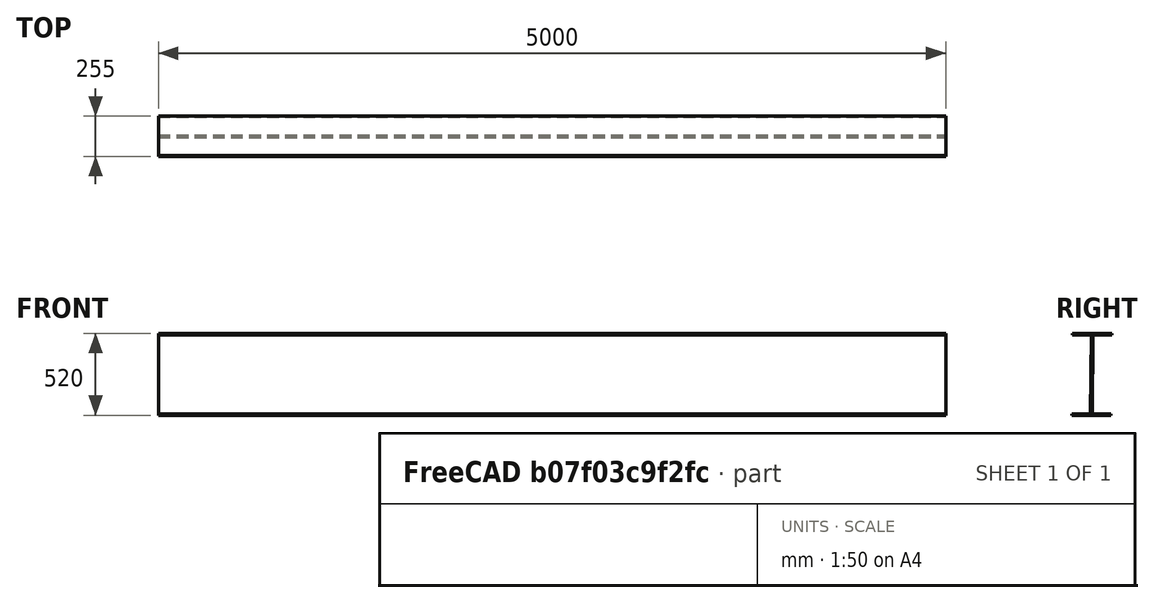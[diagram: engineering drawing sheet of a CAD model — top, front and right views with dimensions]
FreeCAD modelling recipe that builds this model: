
FCSTD DOCUMENT  (FreeCAD 0.21R33694 (Git))
Label: Plate_Girder
License: All rights reserved
LicenseURL: http://en.wikipedia.org/wiki/All_rights_reserved
objects: Sketcher::SketchObject×1, Part::Extrusion×1, Fem::ConstraintFixed×1, App::MaterialObjectPython×1, Fem::ConstraintForce×1, Fem::FemSolverObjectPython×1, Fem::FemMeshObjectPython×1, Fem::ConstraintDisplacement×1, Fem::FemAnalysis×1
note: 2 computed .brp shape members not serialized (recipe doc carries the construction recipe); baked Part::Feature solids carry a one-line shape summary decoded from their .brp

FEATURE [Sketcher::SketchObject] Sketch
  FullyConstrained = true
  Placement = pos=(0,0,0) rot=(0.57735,0.57735,0.57735;2.0944rad)
  sketch-geometry (16):
    g0: LineSegment StartX=0 StartY=0 StartZ=0 EndX=120 EndY=0 EndZ=0
    g1: LineSegment StartX=120 StartY=0 StartZ=0 EndX=125 EndY=500 EndZ=0
    g2: LineSegment StartX=125 StartY=500 StartZ=0 EndX=5 EndY=500 EndZ=0
    g3: LineSegment StartX=5 StartY=500 StartZ=0 EndX=5 EndY=510 EndZ=0
    g4: LineSegment StartX=255 StartY=510 StartZ=0 EndX=255 EndY=500 EndZ=0
    g5: LineSegment StartX=255 StartY=500 StartZ=0 EndX=135 EndY=500 EndZ=0
    g6: LineSegment StartX=135 StartY=500 StartZ=0 EndX=130 EndY=0 EndZ=0
    g7: LineSegment StartX=130 StartY=0 StartZ=0 EndX=250 EndY=0 EndZ=0
    g8: LineSegment StartX=250 StartY=0 StartZ=0 EndX=250 EndY=-10 EndZ=0
    g9: LineSegment StartX=0 StartY=-10 StartZ=0 EndX=0 EndY=0 EndZ=0
    g10: LineSegment StartX=250 StartY=-10 StartZ=0 EndX=130 EndY=-10 EndZ=0
    g11: LineSegment StartX=0 StartY=-10 StartZ=0 EndX=120 EndY=-10 EndZ=0
    g12: LineSegment StartX=120 StartY=-10 StartZ=0 EndX=130 EndY=-10 EndZ=0
    g13: LineSegment StartX=255 StartY=510 StartZ=0 EndX=135 EndY=510 EndZ=0
    g14: LineSegment StartX=135 StartY=510 StartZ=0 EndX=125 EndY=510 EndZ=0
    g15: LineSegment StartX=125 StartY=510 StartZ=0 EndX=5 EndY=510 EndZ=0
  constraints (47):
    c: Coincident(g-1,g0)
    c: Horizontal(g0)
    c: Coincident(g0,g1)
    c: Coincident(g1,g2)
    c: Horizontal(g2)
    c: Coincident(g2,g3)
    c: Vertical(g4)
    c: Coincident(g4,g5)
    c: Horizontal(g5)
    c: Coincident(g5,g6)
    c: PointOnObject(g6,g-1)
    c: Coincident(g6,g7)
    c: Coincident(g7,g8)
    c: Vertical(g8)
    c: PointOnObject(g9,g-2)
    c: Coincident(g9,g0)
    c: DistanceX(g0,g6) = 10
    c: DistanceY(g4,g4) = 10
    c: Vertical(g3)
    c: DistanceY(g3,g3) = 10
    c: DistanceX(g2,g2) = 120
    c: DistanceX(g5,g5) = 120
    c: DistanceX(g7,g7) = 120
    c: DistanceX(g0,g0) = 120
    c: DistanceY(g8,g8) = 10
    c: Horizontal(g7)
    c: DistanceY(g6,g6) = 500
    c: DistanceX(g0,g1) = 5
    c: DistanceX(g1,g5) = 10
    c: Coincident(g10,g8)
    c: Horizontal(g10)
    c: Coincident(g11,g9)
    c: Horizontal(g11)
    c: Coincident(g12,g11)
    c: Coincident(g12,g10)
    c: Horizontal(g12)
    c: DistanceX(g11,g11) = 120
    c: DistanceX(g10,g10) = 120
    c: Coincident(g13,g4)
    c: Horizontal(g13)
    c: Coincident(g14,g13)
    c: Horizontal(g14)
    c: Coincident(g15,g14)
    c: Coincident(g15,g3)
    c: Horizontal(g15)
    c: DistanceX(g13,g13) = 120
    c: DistanceX(g15,g15) = 120
FEATURE [Part::Extrusion] Extrude
  Base = -> Sketch
  Dir = (1,0,0)
  DirMode = 2
  FaceMakerClass = Part::FaceMakerBullseye
  LengthFwd = 5000
  LengthRev = 0
  Solid = true
  Symmetric = false
FEATURE [Fem::ConstraintFixed] ConstraintFixed
  NormalDirection = (-1,0,0)
  Normals = (6) [(-1,0,0),(-1,0,0),(-1,0,0),(-1,0,0),(-1,0,0),(-1,0,0)]
  Points = (6) [(0,255,510),(0,170,-10),(0,170,510),(0,85,-10),(0,85,510),(0,0,-10)]
  References = -> [Extrude]
  Scale = 21
FEATURE [App::MaterialObjectPython] MaterialSolid  # material (typed FeaturePython)
  Category = 0
  Material = AuthorAndLicense=(c) 2014 M. Münch - GNU Lesser General Public License (LGPL),CardName=Steel-St-E-315,Density=7800 kg/m^3,Father=Metal,+13 more (map truncated)
FEATURE [Fem::ConstraintForce] ConstraintForce
  Direction = -> Extrude [Edge15]
  DirectionVector = (0,0,-1)
  Force = 300000
  NormalDirection = (0,0,1)
  Points = (33) [(5000,135,510),(5000,130,510),(5000,125,510),(4500,135,510),(4500,130,510),(4500,125,510),(4000,135,510),(4000,130,510),(4000,125,510),(3500,135,510),+23 more]
  References = -> [Extrude]
  Reversed = true
FEATURE [Fem::FemSolverObjectPython] SolverCcxTools  # FEM object (typed FeaturePython)
  AnalysisType = 0
  BeamShellResultOutput3D = false
  BucklingFactors = 1
  EigenmodeHighLimit = 1000000
  EigenmodeLowLimit = 0
  EigenmodesCount = 10
  GeometricalNonlinearity = 0
  IterationsControlParameterCutb = 0.25,0.5,0.75,0.85,,,1.5,
  IterationsControlParameterIter = 4,8,9,200,10,400,,200,,
  IterationsControlParameterTimeUse = false
  IterationsThermoMechMaximum = 2000
  IterationsUserDefinedIncrementations = false
  IterationsUserDefinedTimeStepLength = false
  MaterialNonlinearity = 0
  MatrixSolverType = 0
  SplitInputWriter = false
  ThermoMechSteadyState = true
  TimeEnd = 1
  TimeInitialStep = 0.01
FEATURE [Fem::FemMeshObjectPython] FEMMeshGmsh  # FEM object (typed FeaturePython)
  Algorithm2D = 0
  Algorithm3D = 0
  CharacteristicLengthMax = 200
  CharacteristicLengthMin = 0
  CoherenceMesh = true
  ElementDimension = 0
  ElementOrder = 1
  GeometryTolerance = 1e-06
  GroupsOfNodes = false
  HighOrderOptimize = 0
  MeshSizeFromCurvature = 12
  OptimizeNetgen = false
  OptimizeStd = true
  Part = -> Extrude
  RecombinationAlgorithm = 0
  Recombine3DAll = false
  RecombineAll = false
  SecondOrderLinear = false
FEATURE [Fem::ConstraintDisplacement] ConstraintDisplacement
  NormalDirection = (1,0,0)
  Normals = (6) [(1,0,0),(1,0,0),(1,0,0),(1,0,0),(1,0,0),(1,0,0)]
  Points = (6) [(5000,255,510),(5000,170,-10),(5000,170,510),(5000,85,-10),(5000,85,510),(5000,0,-10)]
  References = -> [Extrude]
  Scale = 21
  hasXFormula = false
  hasYFormula = false
  hasZFormula = false
  rotxFix = false
  rotxFree = true
  rotyFix = false
  rotyFree = true
  rotzFix = false
  rotzFree = true
  useFlowSurfaceForce = false
  xDisplacement = 0
  xFix = false
  xFree = false
  xRotation = 0
  yDisplacement = 0
  yFix = false
  yFree = true
  yRotation = 0
  zDisplacement = 0
  zFix = false
  zFree = true
  zRotation = 0
FEATURE [Fem::FemAnalysis] Analysis
  Group = -> [ConstraintFixed,FEMMeshGmsh,MaterialSolid,ConstraintForce,SolverCcxTools,ConstraintDisplacement]
